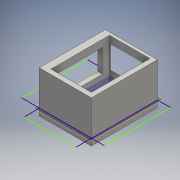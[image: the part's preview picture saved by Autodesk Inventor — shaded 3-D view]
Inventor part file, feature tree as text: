
AUTODESK INVENTOR PART (.ipt)
format: ipt  version: 2016 (Build 200138000, 138)  size: 156,160 bytes
history: native  units: mm
features: sketch x6, extrude x5, plane x1
ambient origin geometry x8: Origin, YZ Plane, XZ Plane, XY Plane, X Axis, Y Axis, Z Axis, Center Point
bodies: Solid1 (feature_tree)
feature tree (12):
  extrude  "Extrusion1"  Depth=56.0mm
  extrude  "Extrusion2"  Depth=71.0mm
  extrude  "Extrusion4"  Depth=7.5mm
  extrude  "Extrusion5"  Depth=5.0mm
  extrude  "Extrusion6"  Depth=50.0mm
  plane  "Work Plane1"
  sketch  "Sketch8"  dims[d12=25.0mm d13=25.0mm d14=12.5mm d15=10.0mm d16=0.0mm d23=57.5mm d24=30.0mm d25=28.75mm d26=10.0mm d27=2.5mm d28=0.0mm d29=10.0mm d30=30.0mm d31=47.5mm d32=23.75mm d33=2.5mm d34=0.0mm d35=40.0mm d36=20.0mm d37=25.0mm d38=12.5mm d39=2.5mm d40=0.0mm d41=-7.5mm]
  sketch  "Sketch1"  dims[d0=56.0mm d1=28.0mm]
  sketch  "Sketch2"  dims[d2=71.0mm d3=35.5mm]
  sketch  "Sketch4"  dims[d4=3.0mm d5=7.5mm]
  sketch  "Sketch5"  dims[d7=5.0mm d8=5.0mm]
  sketch  "Sketch6"  dims[d9=45.0mm d10=0.0mm d11=50.0mm]
